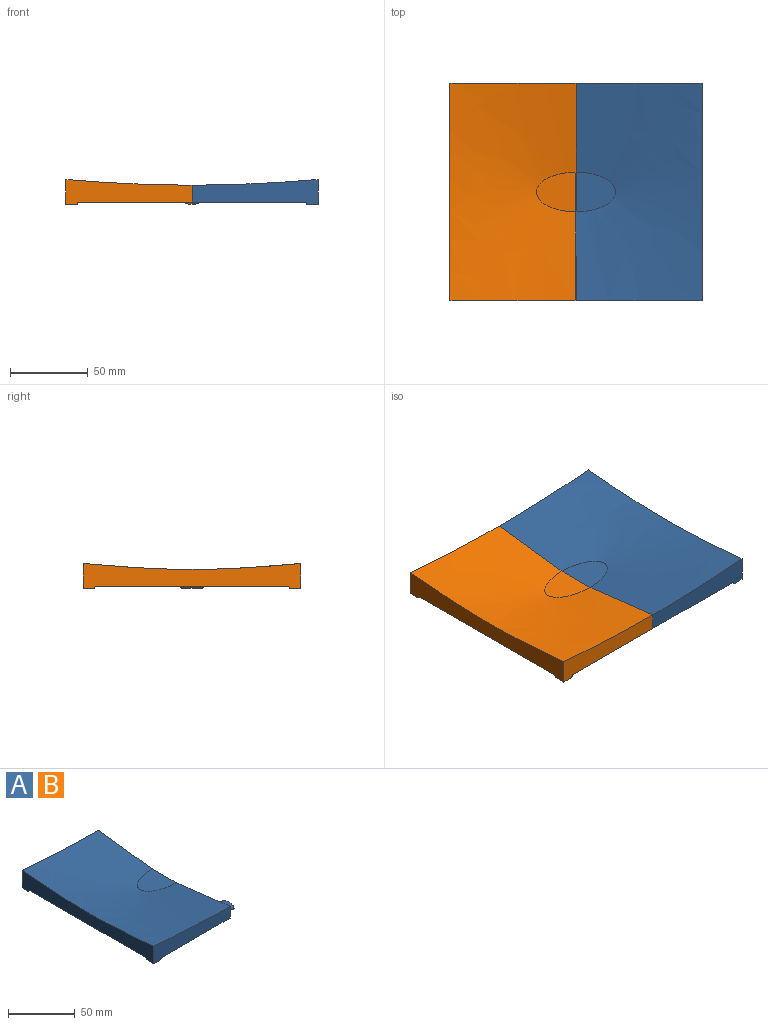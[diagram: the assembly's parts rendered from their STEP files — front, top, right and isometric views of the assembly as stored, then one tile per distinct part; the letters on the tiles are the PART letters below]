
ASSEMBLY  parts=2 mates=1
PART A: 25 faces, bbox 318.5x547.1x61.1 mm
  f0: plane 139.7x80.96mm, normal (0,0,-1), area 11143mm2, adj f1,f2,f3,f4,f11,f12,f14,f15
  f1: plane 139.7x12.41mm, normal (1,0,0), area 840.1mm2, adj f0,f2,f4,f5,f6,f7,f9,f18
  f2: plane 106.19x41.26mm, normal (0,1,0), area 988.5mm2, adj f0,f1,f3,f5,f13,f24
  f3: plane 139.7x16.04mm, normal (-1,0,0), area 1702.6mm2, adj f0,f2,f4,f5,f13,f16,f21,f23
  f4: plane 106.19x41.26mm, normal (0,-1,0), area 988.5mm2, adj f0,f1,f3,f5,f16,f22
  f5: bspline ~521.88x293.25mm, area 12024.3mm2, adj f1,f2,f3,f4,f6
  f6: plane 31.84x31.84mm, normal (0,0,1), area 506.7mm2, adj f1,f5
  f7: extruded ~12.7x8.89mm, area 273.5mm2, adj f1,f8
  f8: plane 12.7x6.35mm, normal (1,0,0), area 63.3mm2, adj f7
  f9: extruded ~11.94x6.35mm, area 180.6mm2, adj f1,f10
  f10: plane 11.94x5.59mm, normal (1,0,0), area 52.4mm2, adj f9
  f11: plane 6.4x1.59mm, normal (1,0,0), area 8mm2, adj f0,f12,f13,f23
  f12: plane 6.4x1.59mm, normal (0,-1,0), area 8mm2, adj f0,f11,f13,f24
  f13: plane 7.17x7.17mm, normal (0,0,-1), area 30mm2, adj f2,f3,f11,f12,f23,f24
  f14: plane 6.4x1.59mm, normal (1,0,0), area 8mm2, adj f0,f15,f16,f21
  f15: plane 6.4x1.59mm, normal (0,1,0), area 8mm2, adj f0,f14,f16,f22
  f16: plane 7.17x7.17mm, normal (0,0,-1), area 30mm2, adj f3,f4,f14,f15,f21,f22
  f17: plane 18.12x3.94mm, normal (-0.5,0,-0.87), area 45.2mm2, adj f0,f18,f19,f20
  f18: plane 13.4x2.54mm, normal (0,0,-1), area 34mm2, adj f1,f17,f19,f20
  f19: cylinder r=1.78mm len=5.29mm, axis (-1,0,0), area 10.2mm2, adj f0,f1,f17,f18
  f20: cylinder r=1.78mm len=5.29mm, axis (-1,0,0), area 10.2mm2, adj f0,f1,f17,f18
  f21: cylinder r=1.78mm len=2.54mm, axis (-1,0,0), area 6.6mm2, adj f0,f3,f14,f16
  f22: cylinder r=1.78mm len=2.54mm, axis (0,1,0), area 6.6mm2, adj f0,f4,f15,f16
  f23: cylinder r=1.78mm len=2.54mm, axis (-1,0,0), area 6.6mm2, adj f0,f3,f11,f13
  f24: cylinder r=1.78mm len=2.54mm, axis (0,-1,0), area 6.6mm2, adj f0,f2,f12,f13
PART B: same geometry as A
PLACE A rot(axis=(0,0,1),180deg) t=(-25.72,-24.93,14.17)mm
PLACE B t=(-25.72,-24.93,14.17)mm fixed
MATE fastened A.f1 <-> B.f1  axis (1,0,0) through (-25.72,44.92,10.36)mm
